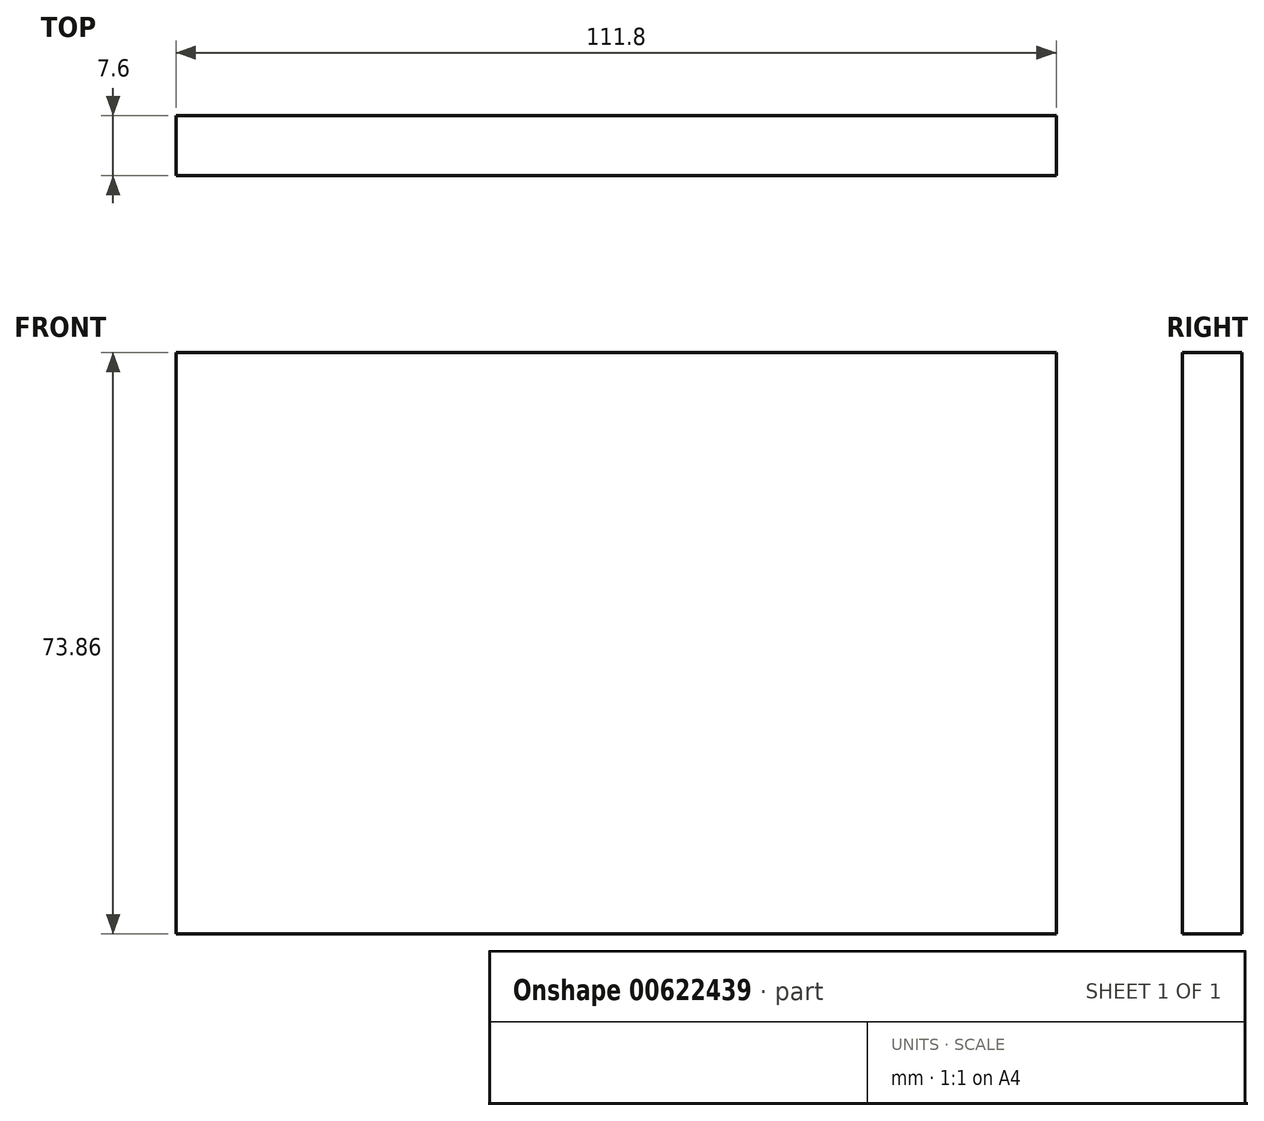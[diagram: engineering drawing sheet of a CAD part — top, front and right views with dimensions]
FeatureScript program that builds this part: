
annotation { "Feature Type Name" : "Feature", "Feature Type Description" : "" }
export const myFeature = defineFeature(function(context is Context, id is Id, definition is map)
    precondition{}
    {
        {
            var Q0;
            Q0=qCreatedBy(makeId("Front.planeOp"),FACE);
            var sketch = newSketch(context, id + "F0", { "sketchPlane" : qUnion([Q0])});
            skLineSegment(sketch, "E0.bottom", {"start": v(-48.65, 73.86) * mm, "end": v(63.15, 73.86) * mm});
            skLineSegment(sketch, "E0.top", {"start": v(-48.65, 0) * mm, "end": v(63.15, 0) * mm});
            skLineSegment(sketch, "E0.left", {"start": v(-48.65, 73.86) * mm, "end": v(-48.65, 0) * mm});
            skLineSegment(sketch, "E0.right", {"start": v(63.15, 73.86) * mm, "end": v(63.15, 0) * mm});
            skSolve(sketch);
        }
        {
            var Q0;
            Q0=makeQuery(id+"F0.imprint","IMPRINT",FACE,{"disambiguationData":[TD([[makeQuery(id+"F0.imprint","IMPRINT",EDGE,{"derivedFrom":sQuery(id+"F0.wireOp",EDGE,"E0.bottom")}),-1.0]])]});
            extrude(context, id + "F1", {"entities" : qUnion([Q0]), "oppositeDirection" : true, "depth" : 7.6 * mm, "offsetDistance" : 25.4 * mm});
        }
    });
